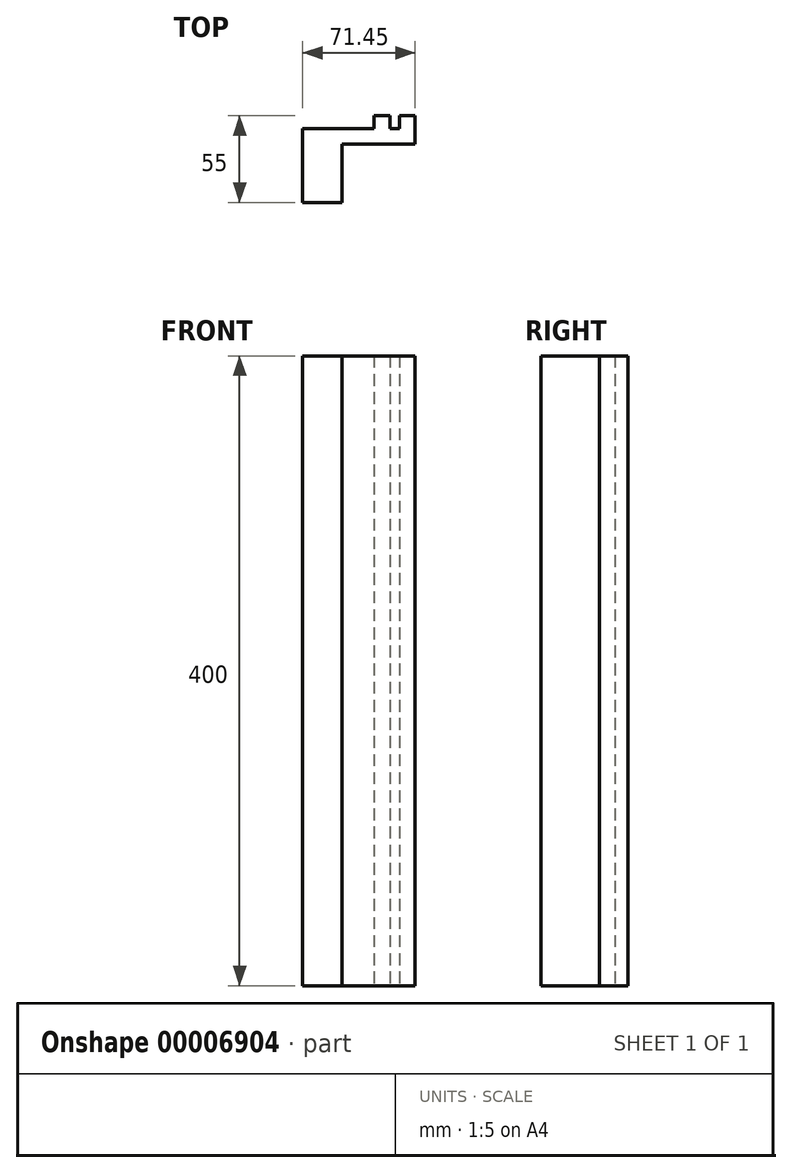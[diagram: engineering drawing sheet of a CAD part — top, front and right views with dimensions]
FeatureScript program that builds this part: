
annotation { "Feature Type Name" : "Feature", "Feature Type Description" : "" }
export const myFeature = defineFeature(function(context is Context, id is Id, definition is map)
    precondition{}
    {
        {
            var Q0;
            Q0=qCreatedBy(makeId("Top.planeOp"),FACE);
            var sketch = newSketch(context, id + "F0", { "sketchPlane" : qUnion([Q0])});
            skLineSegment(sketch, "E0.bottom", {"start": v(0, 0) * mm, "end": v(-25, 0) * mm});
            skLineSegment(sketch, "E0.top", {"start": v(0, 47) * mm, "end": v(-25, 47) * mm});
            skLineSegment(sketch, "E0.left", {"start": v(0, 0) * mm, "end": v(0, 47) * mm});
            skLineSegment(sketch, "E0.right", {"start": v(-25, 0) * mm, "end": v(-25, 47) * mm});
            skLineSegment(sketch, "E1.bottom", {"start": v(-25, 47) * mm, "end": v(46.45, 47) * mm});
            skLineSegment(sketch, "E1.top", {"start": v(-25, 37) * mm, "end": v(46.45, 37) * mm});
            skLineSegment(sketch, "E1.left", {"start": v(-25, 47) * mm, "end": v(-25, 37) * mm});
            skLineSegment(sketch, "E1.right", {"start": v(46.45, 47) * mm, "end": v(46.45, 37) * mm});
            skLineSegment(sketch, "E2.bottom", {"start": v(20.45, 47) * mm, "end": v(30.45, 47) * mm});
            skLineSegment(sketch, "E2.top", {"start": v(20.45, 55) * mm, "end": v(30.45, 55) * mm});
            skLineSegment(sketch, "E2.left", {"start": v(20.45, 47) * mm, "end": v(20.45, 55) * mm});
            skLineSegment(sketch, "E2.right", {"start": v(30.45, 47) * mm, "end": v(30.45, 55) * mm});
            skLineSegment(sketch, "E3.bottom", {"start": v(46.45, 47) * mm, "end": v(36.45, 47) * mm});
            skLineSegment(sketch, "E3.top", {"start": v(46.45, 55) * mm, "end": v(36.45, 55) * mm});
            skLineSegment(sketch, "E3.left", {"start": v(46.45, 47) * mm, "end": v(46.45, 55) * mm});
            skLineSegment(sketch, "E3.right", {"start": v(36.45, 47) * mm, "end": v(36.45, 55) * mm});
            skSolve(sketch);
        }
        {
            var Q0;
            Q0 = qSketchRegion(id + "F0", true);
            extrude(context, id + "F1", {"entities" : qUnion([Q0]), "depth" : (400) * mm});
        }
    });
